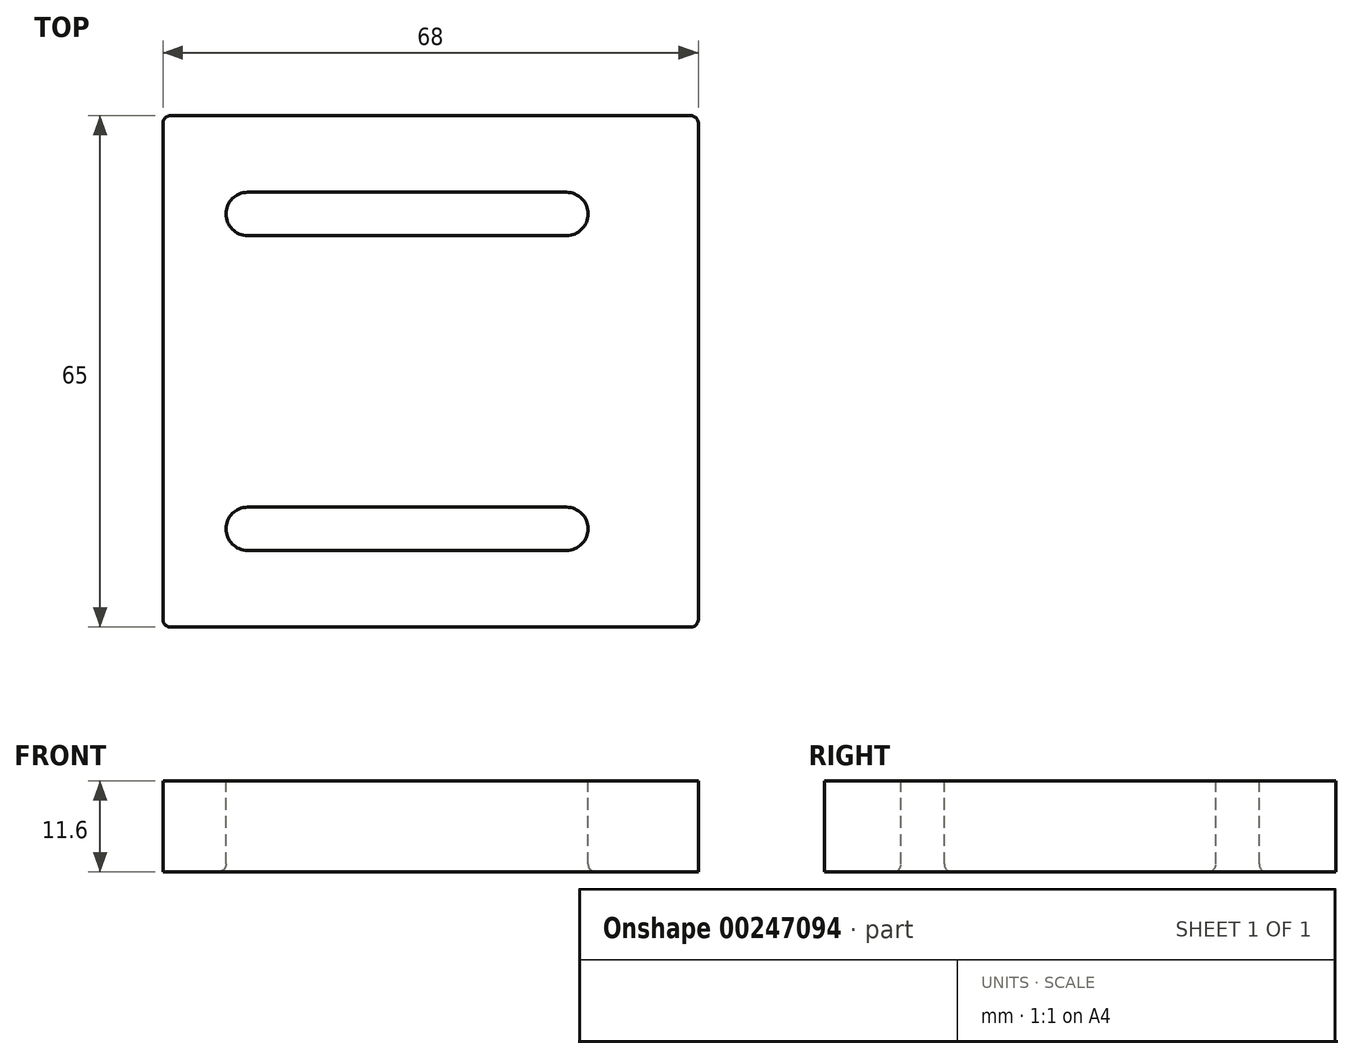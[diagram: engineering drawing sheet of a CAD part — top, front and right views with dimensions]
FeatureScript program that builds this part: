
annotation { "Feature Type Name" : "Feature", "Feature Type Description" : "" }
export const myFeature = defineFeature(function(context is Context, id is Id, definition is map)
    precondition{}
    {
        {
            var Q0;
            Q0=qCreatedBy(makeId("Top.planeOp"),FACE);
            var sketch = newSketch(context, id + "F0", { "sketchPlane" : qUnion([Q0])});
            skLineSegment(sketch, "E0.bottom", {"start": v(0, 0) * mm, "end": v(68, 0) * mm});
            skLineSegment(sketch, "E0.top", {"start": v(0, 65) * mm, "end": v(68, 65) * mm});
            skLineSegment(sketch, "E0.left", {"start": v(0, 0) * mm, "end": v(0, 65) * mm});
            skLineSegment(sketch, "E0.right", {"start": v(68, 0) * mm, "end": v(68, 65) * mm});
            skSolve(sketch);
        }
        {
            var Q0;
            Q0 = qSketchRegion(id + "F0", true);
            extrude(context, id + "F1", {"entities" : qUnion([Q0]), "depth" : 11.6 * mm, "offsetDistance" : 25 * mm});
        }
        {
            var Q0;
            Q0=makeQuery(id+"F1.opExtrude","CAP_FACE",FACE,{"disambiguationData":[OSD([sQuery(id+"F0.wireOp",EDGE,"E0.bottom"),sQuery(id+"F0.wireOp",EDGE,"E0.top"),sQuery(id+"F0.wireOp",EDGE,"E0.left"),sQuery(id+"F0.wireOp",EDGE,"E0.right")])],"isStart":false});
            var sketch = newSketch(context, id + "F2", { "sketchPlane" : qUnion([Q0])});
            skLineSegment(sketch, "E1.bottom", {"start": v(10.75, 15.25) * mm, "end": v(51.25, 15.25) * mm});
            skLineSegment(sketch, "E1.top", {"start": v(10.75, 9.75) * mm, "end": v(51.25, 9.75) * mm});
            skLineSegment(sketch, "E1.left", {"start": v(8, 12.5) * mm, "end": v(8, 12.5) * mm});
            skLineSegment(sketch, "E1.right", {"start": v(54, 12.5) * mm, "end": v(54, 12.5) * mm});
            skPoint(sketch, "E2.visualSharp", {"position": v(8, 15.25) * mm});
            skArc(sketch, "E2.filletArc", {"start": v(10.75, 15.25) * mm, "mid": v(8.8, 14.44) * mm, "end": v(8, 12.5) * mm});
            skPoint(sketch, "E3.visualSharp", {"position": v(8, 9.75) * mm});
            skArc(sketch, "E3.filletArc", {"start": v(8, 12.5) * mm, "mid": v(8.8, 10.56) * mm, "end": v(10.75, 9.75) * mm});
            skPoint(sketch, "E4.visualSharp", {"position": v(54, 9.75) * mm});
            skArc(sketch, "E4.filletArc", {"start": v(51.25, 9.75) * mm, "mid": v(53.2, 10.56) * mm, "end": v(54, 12.5) * mm});
            skPoint(sketch, "E5.visualSharp", {"position": v(54, 15.25) * mm});
            skArc(sketch, "E5.filletArc", {"start": v(54, 12.5) * mm, "mid": v(53.2, 14.44) * mm, "end": v(51.25, 15.25) * mm});
            skLineSegment(sketch, "E6", {"start": v(0, 32.5) * mm, "end": v(74.21, 32.5) * mm, "construction": true});
            skLineSegment(sketch, "E7.MirrorCS", {"start": v(10.75, 55.25) * mm, "end": v(51.25, 55.25) * mm});
            skPoint(sketch, "E8.MirrorP", {"position": v(8, 49.75) * mm});
            skArc(sketch, "E9.MirrorCS", {"start": v(54, 52.5) * mm, "mid": v(53.2, 50.56) * mm, "end": v(51.25, 49.75) * mm});
            skPoint(sketch, "E10.MirrorP", {"position": v(8, 55.25) * mm});
            skLineSegment(sketch, "E11.MirrorCS", {"start": v(54, 52.5) * mm, "end": v(54, 52.5) * mm});
            skPoint(sketch, "E12.MirrorP", {"position": v(54, 55.25) * mm});
            skArc(sketch, "E13.MirrorCS", {"start": v(10.75, 49.75) * mm, "mid": v(8.8, 50.56) * mm, "end": v(8, 52.5) * mm});
            skLineSegment(sketch, "E14.MirrorCS", {"start": v(8, 52.5) * mm, "end": v(8, 52.5) * mm});
            skPoint(sketch, "E15.MirrorP", {"position": v(54, 49.75) * mm});
            skLineSegment(sketch, "E16.MirrorCS", {"start": v(10.75, 49.75) * mm, "end": v(51.25, 49.75) * mm});
            skArc(sketch, "E17.MirrorCS", {"start": v(51.25, 55.25) * mm, "mid": v(53.2, 54.44) * mm, "end": v(54, 52.5) * mm});
            skArc(sketch, "E18.MirrorCS", {"start": v(8, 52.5) * mm, "mid": v(8.8, 54.44) * mm, "end": v(10.75, 55.25) * mm});
            skSolve(sketch);
        }
        {
            var Q0;
            Q0 = qSketchRegion(id + "F2", true);
            extrude(context, id + "F3", {"entities" : qUnion([Q0]), "operationType" : NewBodyOperationType.REMOVE, "oppositeDirection" : true, "depth" : 25 * mm, "offsetDistance" : 25 * mm});
        }
        {
            var Q0;
            Q0=makeQuery(id+"F3.boolean.opBoolean","INTERSECT",EDGE,{"derivedFrom":[makeQuery(id+"F1.opExtrude","CAP_FACE",FACE,{"disambiguationData":[OSD([sQuery(id+"F0.wireOp",EDGE,"E0.bottom"),sQuery(id+"F0.wireOp",EDGE,"E0.top"),sQuery(id+"F0.wireOp",EDGE,"E0.left"),sQuery(id+"F0.wireOp",EDGE,"E0.right")])],"isStart":true}),makeQuery(id+"F3.opExtrude","SWEPT_FACE",FACE,{"disambiguationData":[OSD([sQuery(id+"F2.wireOp",EDGE,"E16.MirrorCS")])]})]});
            var Q1;
            Q1=makeQuery(id+"F3.boolean.opBoolean","INTERSECT",EDGE,{"derivedFrom":[makeQuery(id+"F1.opExtrude","CAP_FACE",FACE,{"disambiguationData":[OSD([sQuery(id+"F0.wireOp",EDGE,"E0.bottom"),sQuery(id+"F0.wireOp",EDGE,"E0.top"),sQuery(id+"F0.wireOp",EDGE,"E0.left"),sQuery(id+"F0.wireOp",EDGE,"E0.right")])],"isStart":true}),makeQuery(id+"F3.opExtrude","SWEPT_FACE",FACE,{"disambiguationData":[OSD([sQuery(id+"F2.wireOp",EDGE,"E1.top")])]})]});
            var Q2;
            Q2=makeQuery(id+"F3.boolean.opBoolean","COPY",EDGE,{"derivedFrom":makeQuery(id+"F3.opExtrude","CAP_EDGE",EDGE,{"disambiguationData":[OSD([sQuery(id+"F2.wireOp",EDGE,"E16.MirrorCS")])],"isStart":true})});
            var Q3;
            Q3=makeQuery(id+"F3.boolean.opBoolean","COPY",EDGE,{"derivedFrom":makeQuery(id+"F3.opExtrude","CAP_EDGE",EDGE,{"disambiguationData":[OSD([sQuery(id+"F2.wireOp",EDGE,"E1.bottom")])],"isStart":true})});
            var Q4;
            Q4=makeQuery(id+"F1.opExtrude","SWEPT_EDGE",EDGE,{"disambiguationData":[OSD([sQuery(id+"F0.wireOp",EDGE,"E0.bottom"),sQuery(id+"F0.wireOp",EDGE,"E0.right")])]});
            var Q5;
            Q5=makeQuery(id+"F1.opExtrude","SWEPT_EDGE",EDGE,{"disambiguationData":[OSD([sQuery(id+"F0.wireOp",EDGE,"E0.top"),sQuery(id+"F0.wireOp",EDGE,"E0.right")])]});
            var Q6;
            Q6=makeQuery(id+"F1.opExtrude","SWEPT_EDGE",EDGE,{"disambiguationData":[OSD([sQuery(id+"F0.wireOp",EDGE,"E0.top"),sQuery(id+"F0.wireOp",EDGE,"E0.left")])]});
            var Q7;
            Q7=makeQuery(id+"F1.opExtrude","SWEPT_EDGE",EDGE,{"disambiguationData":[OSD([sQuery(id+"F0.wireOp",EDGE,"E0.bottom"),sQuery(id+"F0.wireOp",EDGE,"E0.left")])]});
            fillet(context, id + "F4", {"entities" : qUnion([Q0, Q1, Q2, Q3, Q4, Q5, Q6, Q7]), "radius" : 1 * mm, "tangentPropagation" : true, "allowEdgeOverflow" : false});
        }
    });
